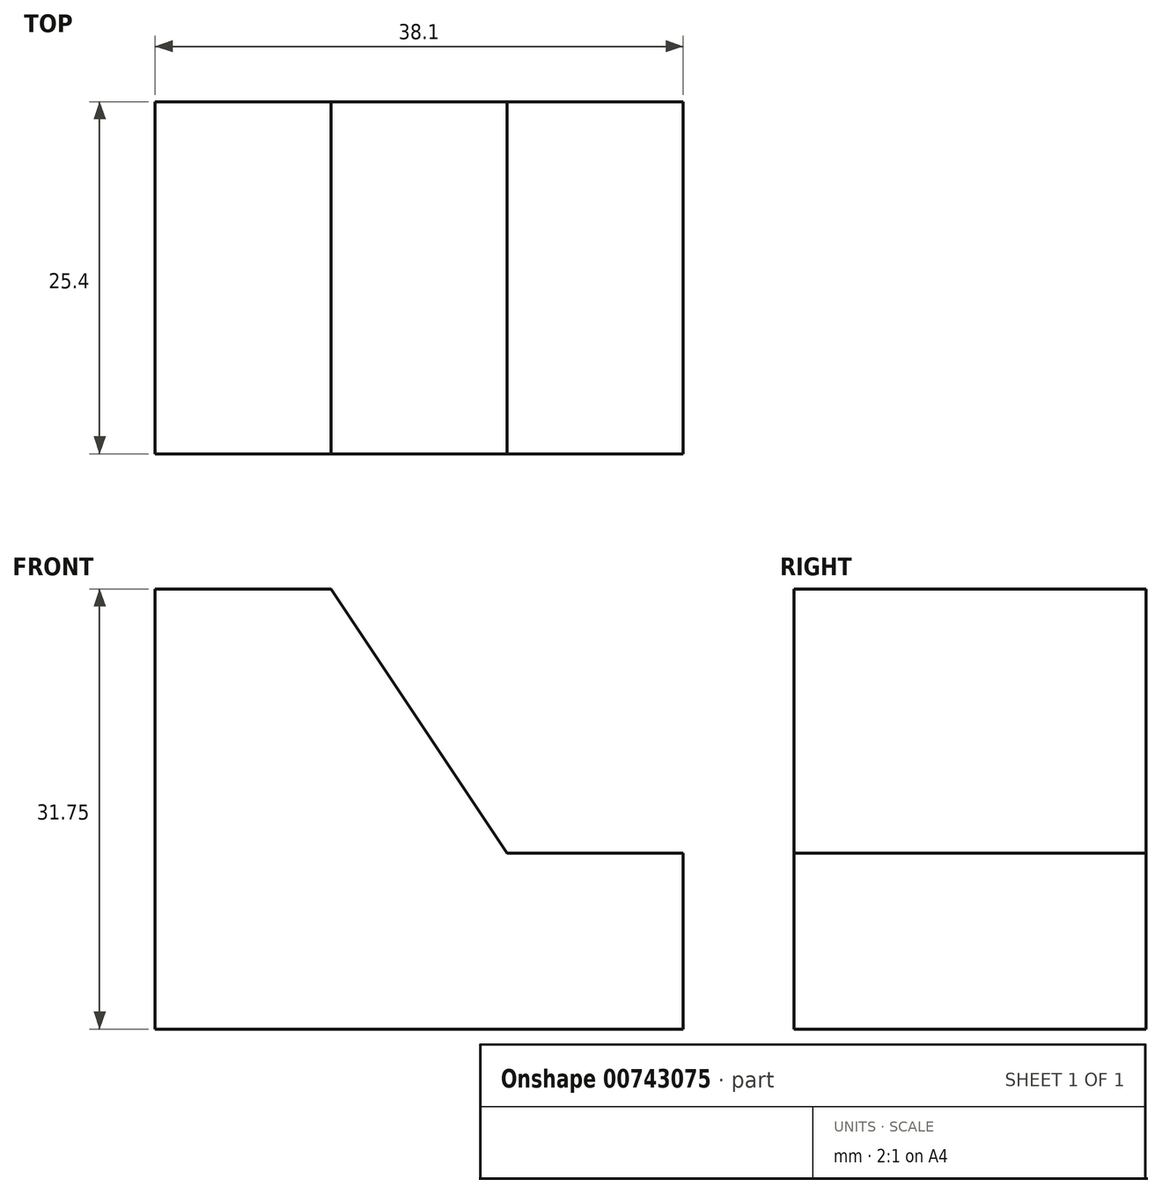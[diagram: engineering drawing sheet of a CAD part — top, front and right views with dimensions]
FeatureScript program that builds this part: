
annotation { "Feature Type Name" : "Feature", "Feature Type Description" : "" }
export const myFeature = defineFeature(function(context is Context, id is Id, definition is map)
    precondition{}
    {
        {
            var Q0;
            Q0=qCreatedBy(makeId("Front.planeOp"),FACE);
            var sketch = newSketch(context, id + "F0", { "sketchPlane" : qUnion([Q0])});
            skLineSegment(sketch, "E0", {"start": v(0, 0) * mm, "end": v(0, 31.75) * mm});
            skLineSegment(sketch, "E1", {"start": v(0, 31.75) * mm, "end": v(12.7, 31.75) * mm});
            skLineSegment(sketch, "E2", {"start": v(38.1, 12.7) * mm, "end": v(38.1, 0) * mm});
            skLineSegment(sketch, "E3", {"start": v(38.1, 0) * mm, "end": v(0, 0) * mm});
            skLineSegment(sketch, "E4", {"start": v(12.7, 31.75) * mm, "end": v(25.4, 12.7) * mm});
            skLineSegment(sketch, "E5", {"start": v(25.4, 12.7) * mm, "end": v(38.1, 12.7) * mm});
            skSolve(sketch);
        }
        {
            var Q0;
            Q0=makeQuery(id+"F0.imprint","IMPRINT",FACE,{"disambiguationData":[TD([[makeQuery(id+"F0.imprint","IMPRINT",EDGE,{"derivedFrom":sQuery(id+"F0.wireOp",EDGE,"E0")}),-1.0]])]});
            extrude(context, id + "F1", {"entities" : qUnion([Q0]), "depth" : 25.4 * mm, "offsetDistance" : 25.4 * mm});
        }
    });
